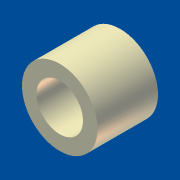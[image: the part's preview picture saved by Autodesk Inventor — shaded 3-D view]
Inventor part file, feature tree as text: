
AUTODESK INVENTOR PART (.ipt)
format: ipt  version: 2013 (Build 170138000, 138)  size: 111,104 bytes
history: native  units: in
note: dims shown in document units (in); Inventor stores cm internally (conversion verified against a paired STEP export)
features: imported_body x1, extrude x1, sketch x1
ambient origin geometry x8: Origin, YZ Plane, XZ Plane, XY Plane, X Axis, Y Axis, Z Axis, Center Point
bodies: Solid1 (feature_tree)
feature tree (3):
  imported_body  "Base1"
  extrude  "Extrusion1"  [1 undecoded]
  sketch  "Sketch1"  dims[d0=0.125in d1=0.0in]
note: 1 required parameter value undecoded (feature->parameter linkage not recoverable at this tier; creation-order binding heuristic only, values carry confidence <= 0.55)
